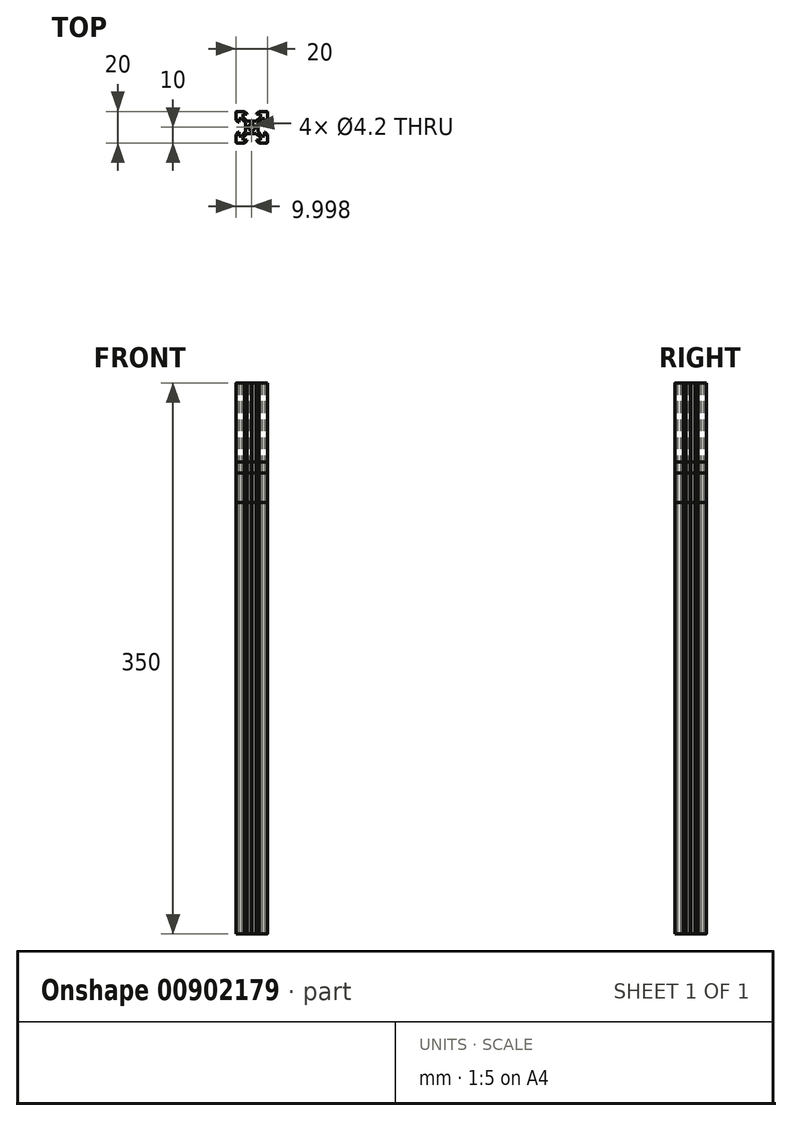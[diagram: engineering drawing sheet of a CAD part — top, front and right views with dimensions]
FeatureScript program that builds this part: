
annotation { "Feature Type Name" : "Feature", "Feature Type Description" : "" }
export const myFeature = defineFeature(function(context is Context, id is Id, definition is map)
    precondition{}
    {
        {
            var Q0;
            Q0=qCreatedBy(makeId("Top.planeOp"),FACE);
            var sketch = newSketch(context, id + "F0", { "sketchPlane" : qUnion([Q0])});
            skLineSegment(sketch, "E0.bottom", {"start": v(-9.51, 10) * mm, "end": v(-4.6, 10) * mm});
            skLineSegment(sketch, "E0.top", {"start": v(-9.51, -10) * mm, "end": v(-4.6, -10) * mm});
            skLineSegment(sketch, "E0.left", {"start": v(-10.01, 9.5) * mm, "end": v(-10.01, 4.58) * mm});
            skLineSegment(sketch, "E0.right", {"start": v(9.99, 9.5) * mm, "end": v(9.99, 4.58) * mm});
            skLineSegment(sketch, "E1", {"start": v(-10.01, 10) * mm, "end": v(9.99, -10) * mm, "construction": true});
            skLineSegment(sketch, "E2", {"start": v(-10.01, 0) * mm, "end": v(9.99, 0) * mm, "construction": true});
            skLineSegment(sketch, "E3", {"start": v(-10.01, 4.58) * mm, "end": v(-8.56, 3.13) * mm});
            skLineSegment(sketch, "E4", {"start": v(-8.56, 3.13) * mm, "end": v(-8.21, 3.13) * mm});
            skLineSegment(sketch, "E5", {"start": v(-8.21, 3.13) * mm, "end": v(-8.21, 5.5) * mm});
            skLineSegment(sketch, "E6", {"start": v(-8.21, 5.5) * mm, "end": v(-6.57, 5.5) * mm});
            skLineSegment(sketch, "E7", {"start": v(-6.57, 5.5) * mm, "end": v(-3.91, 2.84) * mm});
            skLineSegment(sketch, "E8", {"start": v(-3.91, 2.84) * mm, "end": v(-3.91, 0.21) * mm});
            skLineSegment(sketch, "E9", {"start": v(-3.91, 0.21) * mm, "end": v(-3.7, 0) * mm});
            skLineSegment(sketch, "E10.MirrorCS", {"start": v(-10.01, -4.58) * mm, "end": v(-8.56, -3.12) * mm});
            skLineSegment(sketch, "E11.MirrorCS", {"start": v(-8.56, -3.12) * mm, "end": v(-8.21, -3.12) * mm});
            skLineSegment(sketch, "E12.MirrorCS", {"start": v(-8.21, -3.12) * mm, "end": v(-8.21, -5.5) * mm});
            skLineSegment(sketch, "E13.MirrorCS", {"start": v(-8.21, -5.5) * mm, "end": v(-6.57, -5.5) * mm});
            skLineSegment(sketch, "E14.MirrorCS", {"start": v(-6.57, -5.5) * mm, "end": v(-3.91, -2.84) * mm});
            skLineSegment(sketch, "E15.MirrorCS", {"start": v(-3.91, -2.84) * mm, "end": v(-3.91, -0.2) * mm});
            skLineSegment(sketch, "E16.MirrorCS", {"start": v(-3.91, -0.2) * mm, "end": v(-3.7, 0) * mm});
            skLineSegment(sketch, "E17.MirrorCS", {"start": v(2.83, 3.9) * mm, "end": v(0.2, 3.9) * mm});
            skLineSegment(sketch, "E18.MirrorCS", {"start": v(-2.85, 3.9) * mm, "end": v(-0.22, 3.9) * mm});
            skLineSegment(sketch, "E19.MirrorCS", {"start": v(-5.51, 6.56) * mm, "end": v(-2.85, 3.9) * mm});
            skLineSegment(sketch, "E20.MirrorCS", {"start": v(-5.51, 8.2) * mm, "end": v(-5.51, 6.56) * mm});
            skLineSegment(sketch, "E21.MirrorCS", {"start": v(-3.14, 8.2) * mm, "end": v(-5.51, 8.2) * mm});
            skLineSegment(sketch, "E22.MirrorCS", {"start": v(-4.6, 10) * mm, "end": v(-3.14, 8.55) * mm});
            skLineSegment(sketch, "E23.MirrorCS", {"start": v(4.57, 10) * mm, "end": v(3.11, 8.55) * mm});
            skLineSegment(sketch, "E24.MirrorCS", {"start": v(3.11, 8.2) * mm, "end": v(5.49, 8.2) * mm});
            skLineSegment(sketch, "E25.MirrorCS", {"start": v(5.49, 8.2) * mm, "end": v(5.49, 6.56) * mm});
            skLineSegment(sketch, "E26.MirrorCS", {"start": v(5.49, 6.56) * mm, "end": v(2.83, 3.9) * mm});
            skLineSegment(sketch, "E27.MirrorCS", {"start": v(-0.22, 3.9) * mm, "end": v(-0.01, 3.7) * mm});
            skLineSegment(sketch, "E28.MirrorCS", {"start": v(0.2, 3.9) * mm, "end": v(-0.01, 3.7) * mm});
            skLineSegment(sketch, "E29.MirrorCS", {"start": v(-3.14, 8.55) * mm, "end": v(-3.14, 8.2) * mm});
            skLineSegment(sketch, "E30.MirrorCS", {"start": v(3.11, 8.55) * mm, "end": v(3.11, 8.2) * mm});
            skLineSegment(sketch, "E31.MirrorCS", {"start": v(-5.51, -6.56) * mm, "end": v(-2.85, -3.9) * mm});
            skLineSegment(sketch, "E32.MirrorCS", {"start": v(-5.51, -8.2) * mm, "end": v(-5.51, -6.56) * mm});
            skLineSegment(sketch, "E33.MirrorCS", {"start": v(-3.14, -8.2) * mm, "end": v(-5.51, -8.2) * mm});
            skLineSegment(sketch, "E34.MirrorCS", {"start": v(-4.6, -10) * mm, "end": v(-3.14, -8.54) * mm});
            skLineSegment(sketch, "E35.MirrorCS", {"start": v(-3.14, -8.54) * mm, "end": v(-3.14, -8.2) * mm});
            skLineSegment(sketch, "E36.MirrorCS", {"start": v(-0.22, -3.9) * mm, "end": v(-0.01, -3.69) * mm});
            skLineSegment(sketch, "E37.MirrorCS", {"start": v(0.2, -3.9) * mm, "end": v(-0.01, -3.69) * mm});
            skLineSegment(sketch, "E38.MirrorCS", {"start": v(-2.85, -3.9) * mm, "end": v(-0.22, -3.9) * mm});
            skLineSegment(sketch, "E39.MirrorCS", {"start": v(2.83, -3.9) * mm, "end": v(0.2, -3.9) * mm});
            skLineSegment(sketch, "E40.MirrorCS", {"start": v(5.49, -6.56) * mm, "end": v(2.83, -3.9) * mm});
            skLineSegment(sketch, "E41.MirrorCS", {"start": v(5.49, -8.2) * mm, "end": v(5.49, -6.56) * mm});
            skLineSegment(sketch, "E42.MirrorCS", {"start": v(3.11, -8.2) * mm, "end": v(5.49, -8.2) * mm});
            skLineSegment(sketch, "E43.MirrorCS", {"start": v(4.57, -10) * mm, "end": v(3.11, -8.54) * mm});
            skLineSegment(sketch, "E44.MirrorCS", {"start": v(3.11, -8.54) * mm, "end": v(3.11, -8.2) * mm});
            skLineSegment(sketch, "E45.MirrorCS", {"start": v(9.99, 4.58) * mm, "end": v(8.53, 3.13) * mm});
            skLineSegment(sketch, "E46.MirrorCS", {"start": v(8.19, 3.13) * mm, "end": v(8.19, 5.5) * mm});
            skLineSegment(sketch, "E47.MirrorCS", {"start": v(8.19, 5.5) * mm, "end": v(6.55, 5.5) * mm});
            skLineSegment(sketch, "E48.MirrorCS", {"start": v(6.55, 5.5) * mm, "end": v(3.89, 2.84) * mm});
            skLineSegment(sketch, "E49.MirrorCS", {"start": v(3.89, 2.84) * mm, "end": v(3.89, 0.21) * mm});
            skLineSegment(sketch, "E50.MirrorCS", {"start": v(3.89, -2.84) * mm, "end": v(3.89, -0.2) * mm});
            skLineSegment(sketch, "E51.MirrorCS", {"start": v(6.55, -5.5) * mm, "end": v(3.89, -2.84) * mm});
            skLineSegment(sketch, "E52.MirrorCS", {"start": v(8.19, -5.5) * mm, "end": v(6.55, -5.5) * mm});
            skLineSegment(sketch, "E53.MirrorCS", {"start": v(8.19, -3.12) * mm, "end": v(8.19, -5.5) * mm});
            skLineSegment(sketch, "E54.MirrorCS", {"start": v(9.99, -4.58) * mm, "end": v(8.53, -3.12) * mm});
            skLineSegment(sketch, "E55.MirrorCS", {"start": v(8.53, -3.12) * mm, "end": v(8.19, -3.12) * mm});
            skLineSegment(sketch, "E56.MirrorCS", {"start": v(8.53, 3.13) * mm, "end": v(8.19, 3.13) * mm});
            skLineSegment(sketch, "E57.MirrorCS", {"start": v(3.89, 0.21) * mm, "end": v(3.68, 0) * mm});
            skLineSegment(sketch, "E58.MirrorCS", {"start": v(3.89, -0.2) * mm, "end": v(3.68, 0) * mm});
            skCircle(sketch, "E59", {"center": v(-0.01, 0) * mm, "radius": 2.1 * mm});
            skLineSegment(sketch, "E60", {"start": v(-4.6, 10) * mm, "end": v(4.57, 10) * mm, "construction": true});
            skLineSegment(sketch, "E61", {"start": v(4.57, 10) * mm, "end": v(9.49, 10) * mm});
            skLineSegment(sketch, "E62", {"start": v(9.99, 4.58) * mm, "end": v(9.99, -4.58) * mm, "construction": true});
            skLineSegment(sketch, "E63", {"start": v(9.99, -4.58) * mm, "end": v(9.99, -9.5) * mm});
            skLineSegment(sketch, "E64", {"start": v(4.57, -10) * mm, "end": v(9.49, -10) * mm});
            skLineSegment(sketch, "E65", {"start": v(-4.6, -10) * mm, "end": v(4.57, -10) * mm, "construction": true});
            skLineSegment(sketch, "E66", {"start": v(-10.01, -4.58) * mm, "end": v(-10.01, -9.5) * mm});
            skLineSegment(sketch, "E67", {"start": v(-10.01, 4.58) * mm, "end": v(-10.01, -4.58) * mm, "construction": true});
            skPoint(sketch, "E68.visualSharp", {"position": v(-10.01, 10) * mm});
            skArc(sketch, "E68.filletArc", {"start": v(-9.51, 10) * mm, "mid": v(-9.87, 9.85) * mm, "end": v(-10.01, 9.5) * mm});
            skPoint(sketch, "E69.visualSharp", {"position": v(9.99, 10) * mm});
            skArc(sketch, "E69.filletArc", {"start": v(9.99, 9.5) * mm, "mid": v(9.84, 9.85) * mm, "end": v(9.49, 10) * mm});
            skPoint(sketch, "E70.visualSharp", {"position": v(9.99, -10) * mm});
            skArc(sketch, "E70.filletArc", {"start": v(9.49, -10) * mm, "mid": v(9.84, -9.85) * mm, "end": v(9.99, -9.5) * mm});
            skPoint(sketch, "E71.visualSharp", {"position": v(-10.01, -10) * mm});
            skArc(sketch, "E71.filletArc", {"start": v(-10.01, -9.5) * mm, "mid": v(-9.87, -9.85) * mm, "end": v(-9.51, -10) * mm});
            skSolve(sketch);
        }
        {
            var Q0;
            Q0=qSketchRegion(id+"F0",true);
            extrude(context, id + "F1", {"entities" : qUnion([Q0]), "depth" : 300 * mm, "offsetDistance" : 25 * mm});
        }
        {
            var Q0;
            Q0=qSketchRegion(id+"F0",true);
            extrude(context, id + "F2", {"entities" : qUnion([Q0]), "depth" : 293 * mm, "offsetDistance" : 25 * mm});
        }
        {
            var Q0;
            Q0=qSketchRegion(id+"F0",true);
            extrude(context, id + "F3", {"entities" : qUnion([Q0]), "depth" : 274 * mm, "offsetDistance" : 25 * mm});
        }
        {
            var Q0;
            Q0=qSketchRegion(id+"F0",true);
            extrude(context, id + "F4", {"entities" : qUnion([Q0]), "depth" : 350 * mm, "offsetDistance" : 25 * mm});
        }
    });
